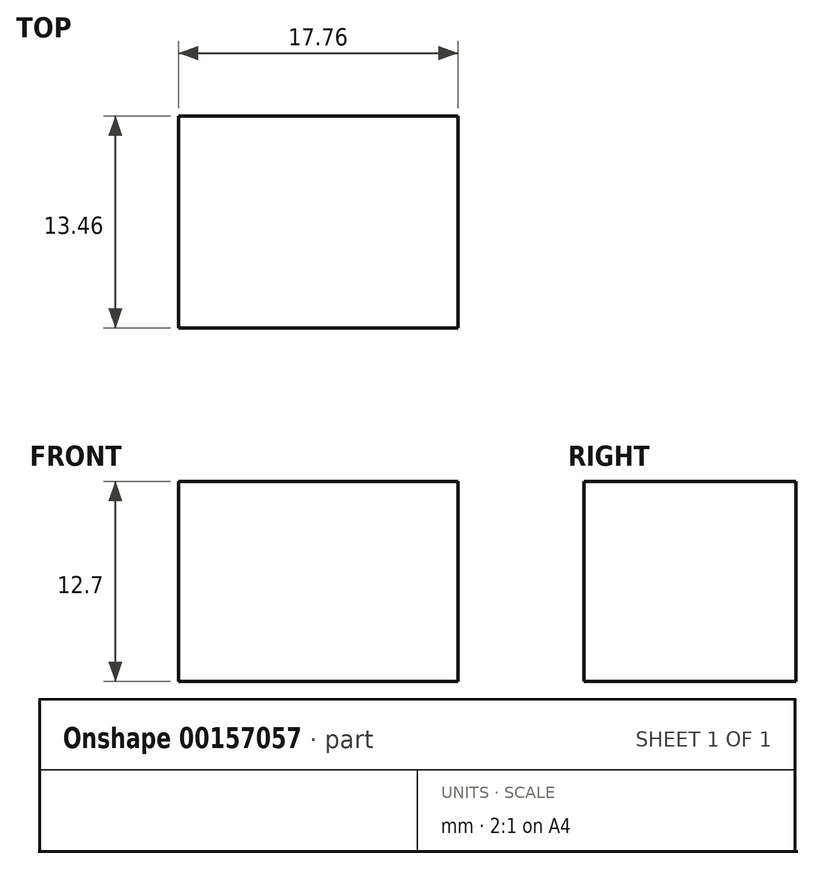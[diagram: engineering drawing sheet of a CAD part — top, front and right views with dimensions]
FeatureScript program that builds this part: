
annotation { "Feature Type Name" : "Feature", "Feature Type Description" : "" }
export const myFeature = defineFeature(function(context is Context, id is Id, definition is map)
    precondition{}
    {
        {
            var Q0;
            Q0=qCreatedBy(makeId("Top.planeOp"),FACE);
            var sketch = newSketch(context, id + "F0", { "sketchPlane" : qUnion([Q0])});
            skLineSegment(sketch, "E0.bottom", {"start": v(8.88, 6.73) * mm, "end": v(-8.88, 6.73) * mm});
            skLineSegment(sketch, "E0.top", {"start": v(8.88, -6.73) * mm, "end": v(-8.88, -6.73) * mm});
            skLineSegment(sketch, "E0.left", {"start": v(8.88, 6.73) * mm, "end": v(8.88, -6.73) * mm});
            skLineSegment(sketch, "E0.right", {"start": v(-8.88, 6.73) * mm, "end": v(-8.88, -6.73) * mm});
            skPoint(sketch, "E0.middle", {"position": v(0, 0) * mm});
            skSolve(sketch);
        }
        {
            var Q0;
            Q0 = qSketchRegion(id + "F0", true);
            extrude(context, id + "F1", {"entities" : qUnion([Q0]), "depth" : 12.7 * mm});
        }
    });
